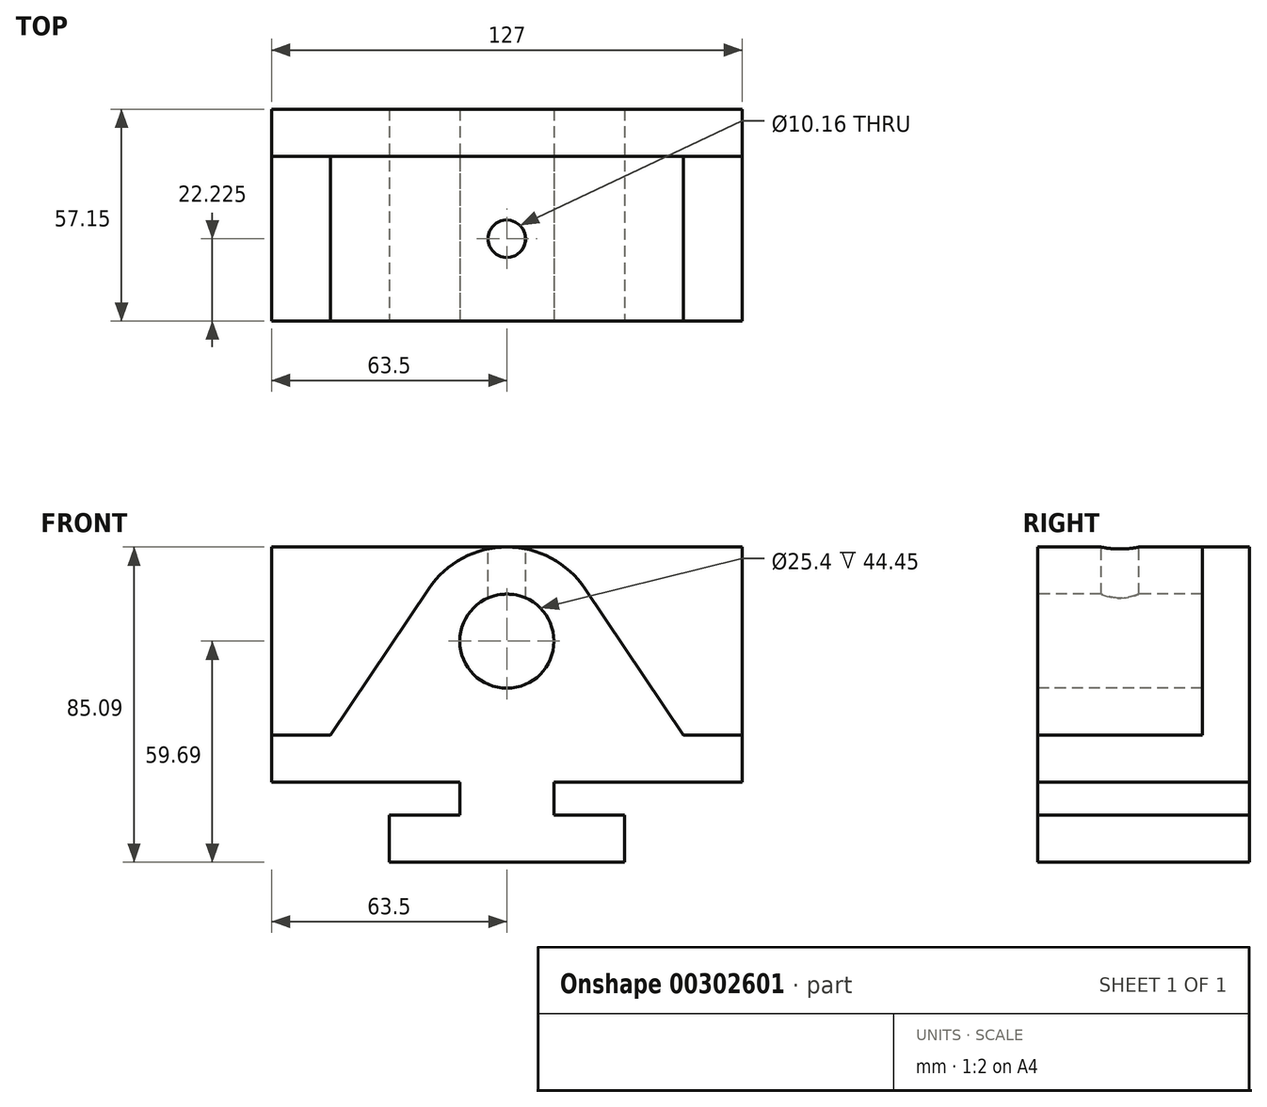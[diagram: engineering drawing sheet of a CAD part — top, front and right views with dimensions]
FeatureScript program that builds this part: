
annotation { "Feature Type Name" : "Feature", "Feature Type Description" : "" }
export const myFeature = defineFeature(function(context is Context, id is Id, definition is map)
    precondition{}
    {
        {
            var Q0;
            Q0=qCreatedBy(makeId("Front.planeOp"),FACE);
            var sketch = newSketch(context, id + "F0", { "sketchPlane" : qUnion([Q0])});
            skLineSegment(sketch, "E0.bottom", {"start": v(0, 0) * mm, "end": v(127, 0) * mm});
            skLineSegment(sketch, "E0.top", {"start": v(0, 85.1) * mm, "end": v(127, 85.1) * mm});
            skLineSegment(sketch, "E0.left", {"start": v(0, 0) * mm, "end": v(0, 85.1) * mm});
            skLineSegment(sketch, "E0.right", {"start": v(127, 0) * mm, "end": v(127, 85.1) * mm});
            skSolve(sketch);
        }
        {
            var Q0;
            Q0=makeQuery(id+"F0.imprint","IMPRINT",FACE,{"disambiguationData":[TD([[makeQuery(id+"F0.imprint","IMPRINT",EDGE,{"derivedFrom":sQuery(id+"F0.wireOp",EDGE,"E0.bottom")}),1.0]])]});
            extrude(context, id + "F1", {"entities" : qUnion([Q0]), "depth" : 57.15 * mm});
        }
        {
            var Q0;
            Q0=makeQuery(id+"F1.opExtrude","CAP_FACE",FACE,{"disambiguationData":[OSD([sQuery(id+"F0.wireOp",EDGE,"E0.bottom"),sQuery(id+"F0.wireOp",EDGE,"E0.top"),sQuery(id+"F0.wireOp",EDGE,"E0.left"),sQuery(id+"F0.wireOp",EDGE,"E0.right")])],"isStart":false});
            var sketch = newSketch(context, id + "F2", { "sketchPlane" : qUnion([Q0])});
            skLineSegment(sketch, "E1", {"start": v(95.25, 0) * mm, "end": v(127, 0) * mm});
            skLineSegment(sketch, "E2", {"start": v(127, 0) * mm, "end": v(127, 21.6) * mm});
            skLineSegment(sketch, "E3", {"start": v(127, 21.6) * mm, "end": v(76.2, 21.59) * mm});
            skLineSegment(sketch, "E4", {"start": v(76.2, 21.59) * mm, "end": v(76.2, 12.7) * mm});
            skLineSegment(sketch, "E5", {"start": v(76.2, 12.7) * mm, "end": v(95.25, 12.7) * mm});
            skLineSegment(sketch, "E6", {"start": v(95.25, 12.7) * mm, "end": v(95.25, 0) * mm});
            skLineSegment(sketch, "E7", {"start": v(0, 0) * mm, "end": v(0, 21.6) * mm});
            skLineSegment(sketch, "E8", {"start": v(0, 21.59) * mm, "end": v(50.8, 21.6) * mm});
            skLineSegment(sketch, "E9", {"start": v(50.8, 21.6) * mm, "end": v(50.8, 12.7) * mm});
            skLineSegment(sketch, "E10", {"start": v(50.8, 12.7) * mm, "end": v(31.75, 12.7) * mm});
            skLineSegment(sketch, "E11", {"start": v(31.75, 12.7) * mm, "end": v(31.75, 0) * mm});
            skLineSegment(sketch, "E12", {"start": v(31.75, 0) * mm, "end": v(0, 0) * mm});
            skLineSegment(sketch, "E13", {"start": v(127, 34.3) * mm, "end": v(111.12, 34.3) * mm});
            skLineSegment(sketch, "E14", {"start": v(0, 34.29) * mm, "end": v(15.88, 34.29) * mm});
            skLineSegment(sketch, "E15", {"start": v(15.87, 34.29) * mm, "end": v(42.4, 73.84) * mm});
            skLineSegment(sketch, "E16", {"start": v(111.12, 34.29) * mm, "end": v(84.6, 73.84) * mm});
            skArc(sketch, "E17", {"start": v(42.4, 73.84) * mm, "mid": v(63.5, 85.1) * mm, "end": v(84.6, 73.84) * mm});
            skSolve(sketch);
        }
        {
            var Q0;
            Q0=makeQuery(id+"F2.imprint","IMPRINT",FACE,{"disambiguationData":[TD([[makeQuery(id+"F2.imprint","IMPRINT",EDGE,{"derivedFrom":sQuery(id+"F2.wireOp",EDGE,"E7")}),-1.0]])]});
            var Q1;
            Q1=makeQuery(id+"F2.imprint","IMPRINT",FACE,{"disambiguationData":[TD([[makeQuery(id+"F2.imprint","IMPRINT",EDGE,{"derivedFrom":sQuery(id+"F2.wireOp",EDGE,"E1")}),1.0]])]});
            extrude(context, id + "F3", {"entities" : qUnion([Q0, Q1]), "operationType" : NewBodyOperationType.REMOVE, "endBound" : BoundingType.THROUGH_ALL, "oppositeDirection" : true, "depth" : 25.4 * mm});
        }
        {
            var Q0;
            {var subQ6=sQuery(id+"F2.wireOp",EDGE,"E14");Q0=makeQuery(id+"F2.imprint","IMPRINT",FACE,{"disambiguationData":[TD([[makeQuery(id+"F2.imprint","IMPRINT",EDGE,{"derivedFrom":subQ6}),1.0]])]});}
            var Q1;
            {var subQ6=sQuery(id+"F2.wireOp",EDGE,"E13");Q1=makeQuery(id+"F2.imprint","IMPRINT",FACE,{"disambiguationData":[TD([[makeQuery(id+"F2.imprint","IMPRINT",EDGE,{"derivedFrom":subQ6}),-1.0]])]});}
            extrude(context, id + "F4", {"entities" : qUnion([Q0, Q1]), "operationType" : NewBodyOperationType.REMOVE, "oppositeDirection" : true, "depth" : 44.45 * mm});
        }
        {
            var Q0;
            {var subQ4=sQuery(id+"F2.wireOp",EDGE,"E3");Q0=makeQuery(id+"F2.imprint","IMPRINT",FACE,{"disambiguationData":[TD([[makeQuery(id+"F2.imprint","IMPRINT",EDGE,{"derivedFrom":subQ4}),-1.0]])]});}
            var sketch = newSketch(context, id + "F5", { "sketchPlane" : qUnion([Q0])});
            skCircle(sketch, "E18", {"center": v(63.5, 59.69) * mm, "radius": 12.7 * mm});
            skSolve(sketch);
        }
        {
            var Q0;
            Q0=makeQuery(id+"F5.imprint","IMPRINT",FACE,{"disambiguationData":[TD([[makeQuery(id+"F5.imprint","IMPRINT",EDGE,{"derivedFrom":sQuery(id+"F5.wireOp",EDGE,"E18")}),1.0]])]});
            extrude(context, id + "F6", {"entities" : qUnion([Q0]), "operationType" : NewBodyOperationType.REMOVE, "oppositeDirection" : true, "depth" : 44.45 * mm});
        }
        {
            var Q0;
            Q0=makeQuery(id+"F1.opExtrude","SWEPT_FACE",FACE,{"disambiguationData":[OSD([sQuery(id+"F0.wireOp",EDGE,"E0.top")])]});
            var sketch = newSketch(context, id + "F7", { "sketchPlane" : qUnion([Q0])});
            skCircle(sketch, "E19", {"center": v(63.5, -34.93) * mm, "radius": 5.08 * mm});
            skSolve(sketch);
        }
        {
            var Q0;
            Q0=makeQuery(id+"F7.imprint","IMPRINT",FACE,{"disambiguationData":[TD([[makeQuery(id+"F7.imprint","IMPRINT",EDGE,{"derivedFrom":sQuery(id+"F7.wireOp",EDGE,"E19")}),1.0]])]});
            extrude(context, id + "F8", {"entities" : qUnion([Q0]), "operationType" : NewBodyOperationType.REMOVE, "endBound" : BoundingType.UP_TO_NEXT, "oppositeDirection" : true, "depth" : 25.4 * mm});
        }
    });
